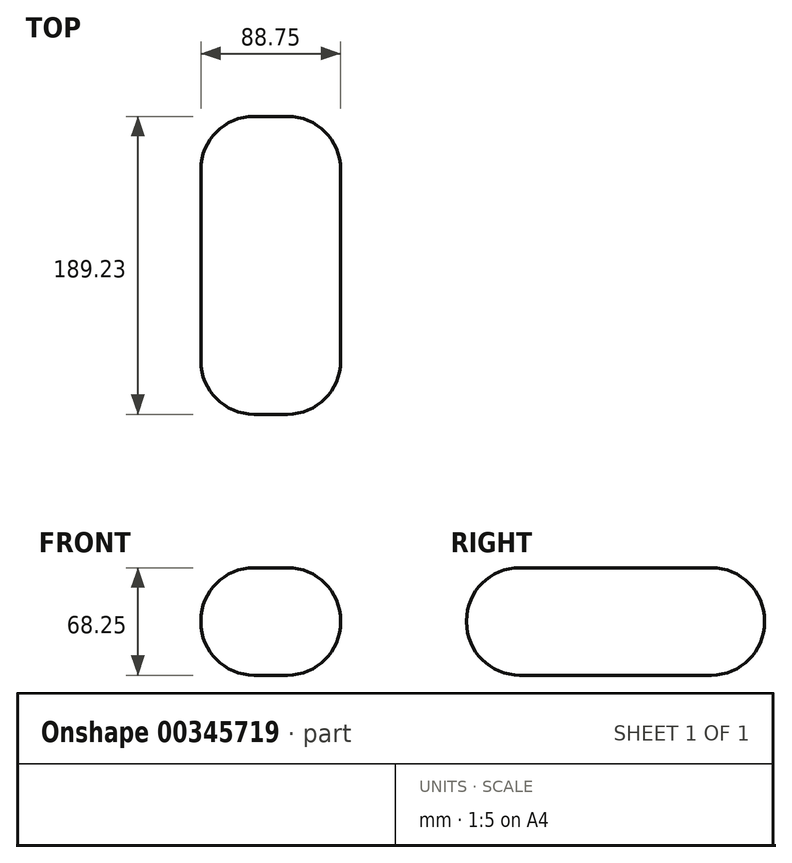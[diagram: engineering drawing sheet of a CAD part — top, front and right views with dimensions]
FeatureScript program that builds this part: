
annotation { "Feature Type Name" : "Feature", "Feature Type Description" : "" }
export const myFeature = defineFeature(function(context is Context, id is Id, definition is map)
    precondition{}
    {
        {
            var Q0;
            Q0=qCreatedBy(makeId("Front.planeOp"),FACE);
            var sketch = newSketch(context, id + "F0", { "sketchPlane" : qUnion([Q0])});
            skLineSegment(sketch, "E0.bottom", {"start": v(-44.57, 30.11) * mm, "end": v(44.18, 30.11) * mm});
            skLineSegment(sketch, "E0.top", {"start": v(-44.57, -38.14) * mm, "end": v(44.18, -38.14) * mm});
            skLineSegment(sketch, "E0.left", {"start": v(-44.57, 30.11) * mm, "end": v(-44.57, -38.14) * mm});
            skLineSegment(sketch, "E0.right", {"start": v(44.18, 30.11) * mm, "end": v(44.18, -38.14) * mm});
            skSolve(sketch);
        }
        {
            var Q0;
            Q0 = qSketchRegion(id + "F0", true);
            extrude(context, id + "F1", {"entities" : qUnion([Q0]), "depth" : 189.23 * mm});
        }
        {
            var Q0;
            Q0=makeQuery(id+"F1.opExtrude","CAP_EDGE",EDGE,{"disambiguationData":[OSD([sQuery(id+"F0.wireOp",EDGE,"E0.bottom")])],"isStart":false});
            var Q1;
            Q1=makeQuery(id+"F1.opExtrude","CAP_EDGE",EDGE,{"disambiguationData":[OSD([sQuery(id+"F0.wireOp",EDGE,"E0.left")])],"isStart":true});
            var Q2;
            Q2=makeQuery(id+"F1.opExtrude","SWEPT_EDGE",EDGE,{"disambiguationData":[OSD([sQuery(id+"F0.wireOp",EDGE,"E0.bottom"),sQuery(id+"F0.wireOp",EDGE,"E0.right")])]});
            var Q3;
            Q3=makeQuery(id+"F1.opExtrude","SWEPT_EDGE",EDGE,{"disambiguationData":[OSD([sQuery(id+"F0.wireOp",EDGE,"E0.top"),sQuery(id+"F0.wireOp",EDGE,"E0.left")])]});
            var Q4;
            Q4=makeQuery(id+"F1.opExtrude","CAP_EDGE",EDGE,{"disambiguationData":[OSD([sQuery(id+"F0.wireOp",EDGE,"E0.right")])],"isStart":true});
            var Q5;
            Q5=makeQuery(id+"F1.opExtrude","CAP_FACE",FACE,{"disambiguationData":[OSD([sQuery(id+"F0.wireOp",EDGE,"E0.bottom"),sQuery(id+"F0.wireOp",EDGE,"E0.top"),sQuery(id+"F0.wireOp",EDGE,"E0.left"),sQuery(id+"F0.wireOp",EDGE,"E0.right")])],"isStart":false});
            var Q6;
            Q6=makeQuery(id+"F1.opExtrude","SWEPT_EDGE",EDGE,{"disambiguationData":[OSD([sQuery(id+"F0.wireOp",EDGE,"E0.top"),sQuery(id+"F0.wireOp",EDGE,"E0.right")])]});
            var Q7;
            Q7=makeQuery(id+"F1.opExtrude","SWEPT_FACE",FACE,{"disambiguationData":[OSD([sQuery(id+"F0.wireOp",EDGE,"E0.bottom")])]});
            var Q8;
            Q8=makeQuery(id+"F1.opExtrude","CAP_EDGE",EDGE,{"disambiguationData":[OSD([sQuery(id+"F0.wireOp",EDGE,"E0.top")])],"isStart":true});
            fillet(context, id + "F2", {"entities" : qUnion([Q0, Q1, Q2, Q3, Q4, Q5, Q6, Q7, Q8]), "radius" : 33.73 * mm, "tangentPropagation" : true, "allowEdgeOverflow" : false});
        }
    });
